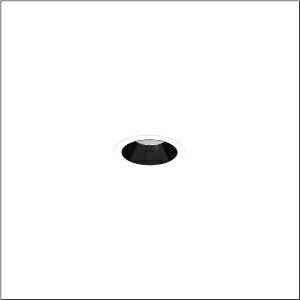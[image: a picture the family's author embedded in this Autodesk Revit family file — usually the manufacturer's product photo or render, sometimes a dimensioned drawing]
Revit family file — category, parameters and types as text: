
# Revit family: lunis_21_s_51db17ea91c
name_source: partatom
category: Lighting Fixtures
units: mm (PartAtom-declared; Revit-internal decimal feet)

## family parameters
Cut with Voids When Loaded = No
Host = Face
Light Source = No
Part Type = Normal
Room Calculation Point = No
Round Connector Dimension = Use Diameter
Shared = No

## types (1)
- --- (1 x LED, 1060 lm, 8 W, 6500K)
    Apparent Load = 8 VA
    CIE Flux Codes = 97 100 100 100 100
    Color Rendering = 80
    Color Temperature = 6500K
    Default Elevation = 1800 mm
    Description = Lunis 21,  S, downlight, light control with lens, of PMMA, anti glare with reflector, of PC, light emission: direct distribution, LED rated luminous flux: 810lm, light colour: 830/840/865, with terminal, 5-pole, mains connection: 220..240V, AC, 50..60Hz, housing, round, of diecast aluminium, traffic white (RAL 9016), diameter: 84mm, clamping range: 1..40mm, protection rating (complete): IP20, protection rating (on room side): IP54, insulation class (complete): insulation class II (safety insulation), certification: CE, impact resistance: IK03, packaging unit: 1 piece
    Height = 0 mm  [stored 0 ft]
    Lamp = 1 x LED
    Lamp Light Flux = 1060 lm
    Lamp Power = 8 W
    Lamp count = 1
    Length = 84 mm
    Luminous efficacy = 133 lm/W
    Manufacturer = Siteco
    ModVariant = No
    Model = 51DB17EA91C
    Mounting Place = Ceiling
    Mounting Type = Recessed
    Number of Poles = 1
    OnlyDefault = Yes
    Power Factor = 1
    Product Name = Lunis 21 S
    Product group = downlight
    ProductGroupID = 400
    Protection Class = Protection class II
    Protection Degree = IP 20
    RLX_Detail_Level = 1
    RLX_Emergency_Light_Flux = 0 lm
    RLX_Emergency_Type = 0
    RLX_Emergency_Type_DB = No
    RlxData = <blob elided: 9789 chars, md5=dcc5bbb7>
    Socket = socket
    Standby Power = 0 W
    System Light Flux = 1060 lm
    System Power = 8 W
    Type Comments = individual setting: colour temperature 6500K, luminous flux: 100 % | (OFF | OFF | ON | OFF) | 200 mA
    Type Image = l_1290844.jpg
    URL = http://relux.com
    VarID = @adj_020216
    Voltage = 0 V
    Weight = 0.00 kg
    Width = 0 mm  [stored 0 ft]

note: [stored X ft] marks values corroborated as IEEE doubles in the binary element streams (Revit-internal decimal feet)

## geometry (parser evidence)
native form markers: Sweep x10
no freeform markers — native parametric forms only
